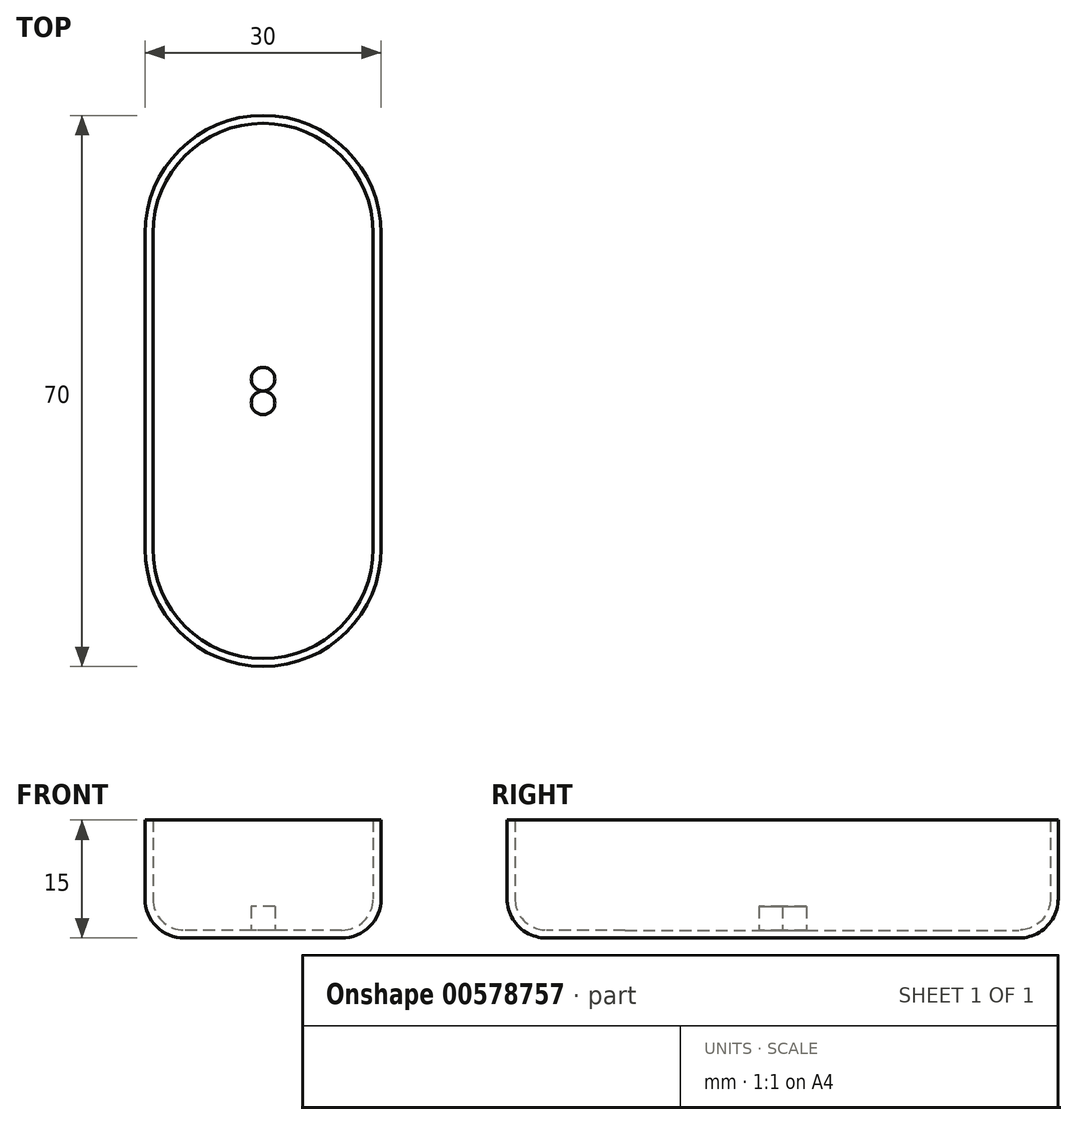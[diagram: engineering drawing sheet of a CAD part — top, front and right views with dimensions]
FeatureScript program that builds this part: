
annotation { "Feature Type Name" : "Feature", "Feature Type Description" : "" }
export const myFeature = defineFeature(function(context is Context, id is Id, definition is map)
    precondition{}
    {
        {
            var Q0;
            Q0=qCreatedBy(makeId("Top.planeOp"),FACE);
            var sketch = newSketch(context, id + "F0", { "sketchPlane" : qUnion([Q0])});
            skCircle(sketch, "E0", {"center": v(0, 0) * mm, "radius": 15 * mm});
            skLineSegment(sketch, "E1", {"start": v(0, 0) * mm, "end": v(0, -40) * mm});
            skCircle(sketch, "E2", {"center": v(0, -40) * mm, "radius": 15 * mm});
            skLineSegment(sketch, "E3", {"start": v(0, 0) * mm, "end": v(-15, 0) * mm});
            skLineSegment(sketch, "E4", {"start": v(-15, 0) * mm, "end": v(-15, -40) * mm});
            skLineSegment(sketch, "E5", {"start": v(-15, -40) * mm, "end": v(15, -40) * mm});
            skLineSegment(sketch, "E6", {"start": v(15, -40) * mm, "end": v(15, 0) * mm});
            skLineSegment(sketch, "E7", {"start": v(15, 0) * mm, "end": v(0, 0) * mm});
            skSolve(sketch);
        }
        {
            var Q0;
            {var subQ0=sQuery(id+"F0.wireOp",EDGE,"E4");Q0=makeQuery(id+"F0.imprint","IMPRINT",FACE,{"disambiguationData":[TD([[makeQuery(id+"F0.imprint","IMPRINT",EDGE,{"derivedFrom":subQ0}),1.0]])]});}
            var Q1;
            {var subQ0=sQuery(id+"F0.wireOp",EDGE,"E3");Q1=makeQuery(id+"F0.imprint","IMPRINT",FACE,{"disambiguationData":[TD([[makeQuery(id+"F0.imprint","IMPRINT",EDGE,{"derivedFrom":subQ0}),1.0]])]});}
            var Q2;
            {var subQ0=sQuery(id+"F0.wireOp",EDGE,"E7");Q2=makeQuery(id+"F0.imprint","IMPRINT",FACE,{"disambiguationData":[TD([[makeQuery(id+"F0.imprint","IMPRINT",EDGE,{"derivedFrom":subQ0}),1.0]])]});}
            var Q3;
            {var subQ0=sQuery(id+"F0.wireOp",EDGE,"E6");Q3=makeQuery(id+"F0.imprint","IMPRINT",FACE,{"disambiguationData":[TD([[makeQuery(id+"F0.imprint","IMPRINT",EDGE,{"derivedFrom":subQ0}),1.0]])]});}
            var Q4;
            {var subQ0=sQuery(id+"F0.wireOp",EDGE,"E5");var subQ1=sQuery(id+"F0.wireOp",EDGE,"E1");var subQ2=makeQuery(id+"F0.imprint","INTERSECT",VERTEX,{"derivedFrom":[subQ1,subQ0]});Q4=makeQuery(id+"F0.imprint","IMPRINT",FACE,{"disambiguationData":[TD([[makeQuery(id+"F0.imprint","IMPRINT",EDGE,{"disambiguationData":[TD([[subQ2,1.0]])],"derivedFrom":subQ1}),1.0]])]});}
            var Q5;
            {var subQ0=sQuery(id+"F0.wireOp",EDGE,"E5");var subQ1=sQuery(id+"F0.wireOp",EDGE,"E1");var subQ2=makeQuery(id+"F0.imprint","INTERSECT",VERTEX,{"derivedFrom":[subQ1,subQ0]});Q5=makeQuery(id+"F0.imprint","IMPRINT",FACE,{"disambiguationData":[TD([[makeQuery(id+"F0.imprint","IMPRINT",EDGE,{"disambiguationData":[TD([[subQ2,1.0]])],"derivedFrom":subQ1}),-1.0]])]});}
            var Q6;
            {var subQ0=sQuery(id+"F0.wireOp",EDGE,"E3");Q6=makeQuery(id+"F0.imprint","IMPRINT",FACE,{"disambiguationData":[TD([[makeQuery(id+"F0.imprint","IMPRINT",EDGE,{"derivedFrom":subQ0}),-1.0]])]});}
            var Q7;
            {var subQ0=sQuery(id+"F0.wireOp",EDGE,"E3");Q7=makeQuery(id+"F0.imprint","IMPRINT",FACE,{"disambiguationData":[TD([[makeQuery(id+"F0.imprint","IMPRINT",EDGE,{"derivedFrom":subQ0}),-1.0]])]});}
            var Q8;
            {var subQ0=sQuery(id+"F0.wireOp",EDGE,"E5");var subQ4=makeQuery(id+"F0.imprint","INTERSECT",VERTEX,{"derivedFrom":[sQuery(id+"F0.wireOp",EDGE,"E1"),subQ0]});Q8=makeQuery(id+"F0.imprint","IMPRINT",FACE,{"disambiguationData":[TD([[makeQuery(id+"F0.imprint","IMPRINT",EDGE,{"disambiguationData":[TD([[subQ4,1.0]])],"derivedFrom":subQ0}),-1.0]])]});}
            extrude(context, id + "F1", {"entities" : qUnion([Q0, Q1, Q2, Q3, Q4, Q5, Q6, Q7, Q8]), "depth" : 15 * mm, "offsetDistance" : 25 * mm});
        }
        {
            var Q0;
            Q0=makeQuery(id+"F1.opExtrude","CAP_EDGE",EDGE,{"disambiguationData":[OSD([sQuery(id+"F0.wireOp",EDGE,"E0")])],"isStart":true});
            fillet(context, id + "F2", {"entities" : qUnion([Q0]), "radius" : 5 * mm, "tangentPropagation" : true, "allowEdgeOverflow" : false});
        }
        {
            var Q0;
            Q0=makeQuery(id+"F1.opExtrude","CAP_FACE",FACE,{"disambiguationData":[OSD([sQuery(id+"F0.wireOp",EDGE,"E0"),sQuery(id+"F0.wireOp",EDGE,"E2"),sQuery(id+"F0.wireOp",EDGE,"E4"),sQuery(id+"F0.wireOp",EDGE,"E6")])],"isStart":false});
            shell(context, id + "F3", {"entities" : qUnion([Q0]), "thickness" : 1 * mm});
        }
        {
            var Q0;
            Q0=makeQuery(id+"F3.opShell","OFFSET_FACE",FACE,{"disambiguationData":[OSD([sQuery(id+"F0.wireOp",EDGE,"E0"),sQuery(id+"F0.wireOp",EDGE,"E2"),sQuery(id+"F0.wireOp",EDGE,"E4"),sQuery(id+"F0.wireOp",EDGE,"E6")])]});
            var sketch = newSketch(context, id + "F4", { "sketchPlane" : qUnion([Q0])});
            skLineSegment(sketch, "E8", {"start": v(0, 0) * mm, "end": v(0, -18.5) * mm});
            skLineSegment(sketch, "E9", {"start": v(0, -18.5) * mm, "end": v(0, -21.5) * mm});
            skCircle(sketch, "E10", {"center": v(0, -18.5) * mm, "radius": 1.5 * mm});
            skCircle(sketch, "E11", {"center": v(0, -21.5) * mm, "radius": 1.5 * mm});
            skSolve(sketch);
        }
        {
            var Q0;
            {var subQ0=sQuery(id+"F4.wireOp",EDGE,"E9");var subQ1=sQuery(id+"F4.wireOp",EDGE,"E8");var subQ2=makeQuery(id+"F4.imprint","INTERSECT",VERTEX,{"derivedFrom":[subQ1,subQ0]});Q0=makeQuery(id+"F4.imprint","IMPRINT",FACE,{"disambiguationData":[TD([[makeQuery(id+"F4.imprint","IMPRINT",EDGE,{"disambiguationData":[TD([[subQ2,1.0]])],"derivedFrom":subQ1}),1.0]])]});}
            var Q1;
            {var subQ0=sQuery(id+"F4.wireOp",EDGE,"E9");var subQ1=sQuery(id+"F4.wireOp",EDGE,"E8");var subQ2=makeQuery(id+"F4.imprint","INTERSECT",VERTEX,{"derivedFrom":[subQ1,subQ0]});Q1=makeQuery(id+"F4.imprint","IMPRINT",FACE,{"disambiguationData":[TD([[makeQuery(id+"F4.imprint","IMPRINT",EDGE,{"disambiguationData":[TD([[subQ2,1.0]])],"derivedFrom":subQ1}),-1.0]])]});}
            var Q2;
            Q2=makeQuery(id+"F4.imprint","IMPRINT",FACE,{"disambiguationData":[TD([[makeQuery(id+"F4.imprint","IMPRINT",EDGE,{"derivedFrom":sQuery(id+"F4.wireOp",EDGE,"E11")}),1.0]])]});
            extrude(context, id + "F5", {"entities" : qUnion([Q0, Q1, Q2]), "depth" : 3 * mm, "offsetDistance" : 25 * mm});
        }
    });
